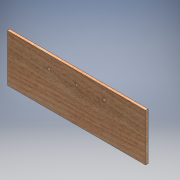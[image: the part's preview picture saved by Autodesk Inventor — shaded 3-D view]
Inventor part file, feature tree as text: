
AUTODESK INVENTOR PART (.ipt)
format: ipt  version: 2016 (Build 200138000, 138)  size: 141,312 bytes
history: native  units: mm
features: sketch x3, extrude x2, hole x1
ambient origin geometry x8: Origin, YZ Plane, XZ Plane, XY Plane, X Axis, Y Axis, Z Axis, Center Point
bodies: Solid1 (feature_tree)
feature tree (6):
  extrude  "Extrusion1"  Depth=120.0mm
  extrude  "Extrusion2"  Depth=31.0mm
  hole  "Hole1"  [1 undecoded]
  sketch  "Sketch1"  dims[d0=350.0mm d1=120.0mm]
  sketch  "Sketch2"  dims[d2=7.5mm d3=31.0mm]
  sketch  "Sketch3"  dims[d4=7.5mm d5=7.5mm d6=70.0mm d7=70.0mm d8=6.35mm d9=0.0mm d10=35.0mm d11=40.0mm d12=157.5mm d13=62.0mm d14=0.0mm d15=4.25mm d16=6.0mm d17=4.25mm d18=6.0mm d19=4.25mm d20=6.0mm d21=4.25mm d22=6.0mm d23=4.0mm d24=2.0mm d25=90.0deg d26=8.0mm d27=20.594885mm]
note: 1 required parameter value undecoded (feature->parameter linkage not recoverable at this tier; creation-order binding heuristic only, values carry confidence <= 0.55)
